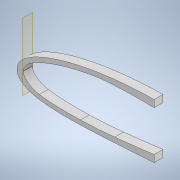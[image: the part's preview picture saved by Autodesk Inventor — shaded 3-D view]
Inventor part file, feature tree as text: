
AUTODESK INVENTOR PART (.ipt)
format: ipt  version: 2022.3 (Build 263350000, 350)  size: 513,024 bytes
history: native  units: mm
features: sketch x6, extrude x5, thicken_offset x3, fillet x2, projected_geometry x2, shell x1, plane x1, other x1
ambient origin geometry x8: Origin, YZ Plane, XZ Plane, XY Plane, X Axis, Y Axis, Z Axis, Center Point
bodies: Solid1 (feature_tree)
feature tree (21):
  extrude  "Extrusion1"  Depth=3.0mm
  shell  "Shell1"  Thickness=1.0mm
  thicken_offset  "Thicken1"
  extrude  "Extrusion27"  TaperAngle=0.0deg  [1 undecoded]
  thicken_offset  "Thicken3"
  extrude  "Extrusion29"  Depth=20.0mm
  plane  "Work Plane5"
  other  "Bend Part2"
  thicken_offset  "Thicken5"
  extrude  "Extrusion30"  Depth=10.0mm TaperAngle=0.0deg
  extrude  "Extrusion31"  Depth=1.0mm
  fillet  "Fillet6"  Radius=1.0mm
  fillet  "Fillet7"  Radius=100.0mm
  sketch  "Sketch3"  dims[d0=10.0mm d1=0.0mm d2=3.0mm d159=1.0mm d160=2.0mm]
  sketch  "Sketch48"  dims[d236=190.0mm d237=0.0mm d238=0.0mm]
  sketch  "Sketch55"  dims[d249=2.0mm d250=1.0mm d254=20.0mm]
  projected_geometry  "Projected Loop32"
  sketch  "Sketch57"  dims[d255=8.0mm d256=10.0mm d257=0.0mm]
  sketch  "Sketch58"  dims[d262=10.0mm d263=0.349066mm d264=1.0mm d265=1.0mm d268=100.0mm]
  projected_geometry  "Projected Loop34"
  sketch  "Sketch59"  dims[d269=5.0mm d270=10.0mm d271=0.0mm d272=150.0mm d273=100.0mm d274=0.0mm d275=550.0mm d276=100.0mm d277=6.0mm d278=2000.0mm d279=500.0mm d280=200.0mm]
note: 1 required parameter value undecoded (feature->parameter linkage not recoverable at this tier; creation-order binding heuristic only, values carry confidence <= 0.55)
